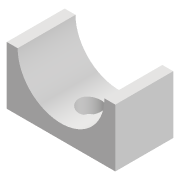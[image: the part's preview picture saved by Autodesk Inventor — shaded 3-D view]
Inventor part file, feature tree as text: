
AUTODESK INVENTOR PART (.ipt)
format: ipt  version: 2022 (Build 260153000, 153)  size: 103,936 bytes
history: native  units: mm
features: extrude x2, sketch x2, projected_geometry x1
ambient origin geometry x8: Origin, YZ Plane, XZ Plane, XY Plane, X Axis, Y Axis, Z Axis, Center Point
bodies: Solid1 (feature_tree)
feature tree (5):
  extrude  "Extrusion1"  Depth=2.0mm
  extrude  "Extrusion2"  Depth=7.5mm
  sketch  "Sketch1"  dims[d0=12.0mm d1=2.0mm]
  sketch  "Sketch2"  dims[d2=7.5mm d3=7.5mm d4=8.0mm d5=0.0mm d6=3.1mm d7=6.0mm d8=0.0mm]
  projected_geometry  "Projected Loop1"
